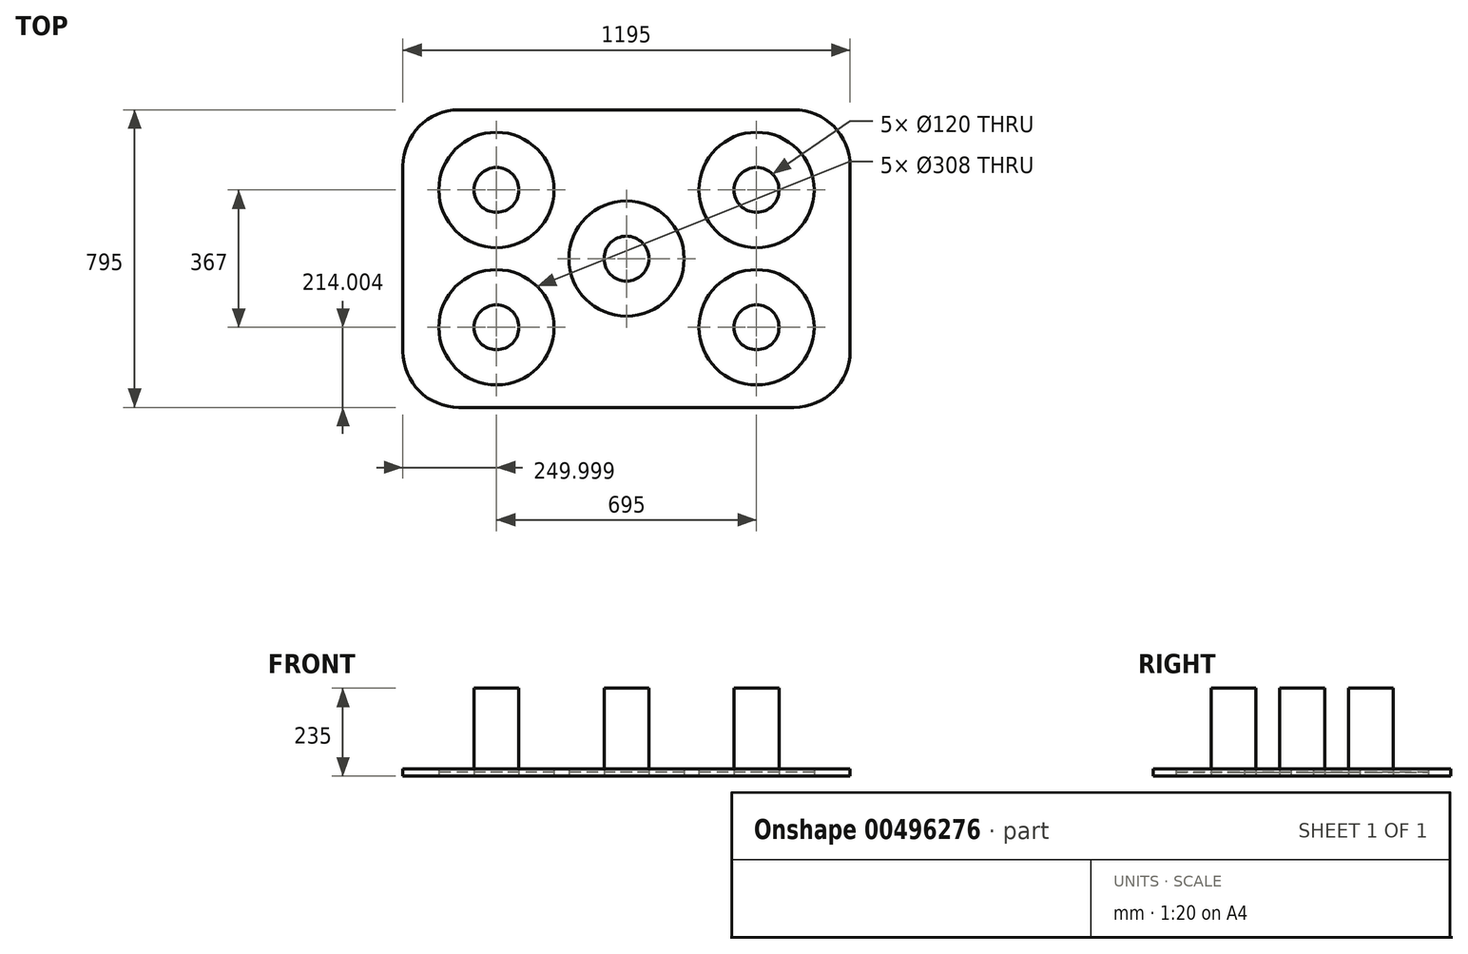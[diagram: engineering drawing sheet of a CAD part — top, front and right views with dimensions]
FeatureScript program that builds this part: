
annotation { "Feature Type Name" : "Feature", "Feature Type Description" : "" }
export const myFeature = defineFeature(function(context is Context, id is Id, definition is map)
    precondition{}
    {
        {
            var Q0;
            Q0=qCreatedBy(makeId("Top.planeOp"),FACE);
            var sketch = newSketch(context, id + "F0", { "sketchPlane" : qUnion([Q0])});
            skLineSegment(sketch, "E0.bottom", {"start": v(51.86, 514.27) * mm, "end": v(946.86, 514.27) * mm});
            skLineSegment(sketch, "E0.top", {"start": v(51.86, -280.73) * mm, "end": v(946.86, -280.73) * mm});
            skLineSegment(sketch, "E0.left", {"start": v(-98.14, 364.27) * mm, "end": v(-98.14, -130.73) * mm});
            skLineSegment(sketch, "E0.right", {"start": v(1096.86, 364.27) * mm, "end": v(1096.86, -130.73) * mm});
            skCircle(sketch, "E1", {"center": v(151.86, 300.27) * mm, "radius": 60 * mm});
            skCircle(sketch, "E2", {"center": v(846.86, -66.73) * mm, "radius": 60 * mm});
            skCircle(sketch, "E3", {"center": v(151.86, -66.73) * mm, "radius": 60 * mm});
            skCircle(sketch, "E4", {"center": v(846.86, 300.27) * mm, "radius": 60 * mm});
            skCircle(sketch, "E5", {"center": v(499.36, 116.77) * mm, "radius": 60 * mm});
            skPoint(sketch, "E6.visualSharp", {"position": v(-98.14, 514.27) * mm});
            skArc(sketch, "E6.filletArc", {"start": v(51.86, 514.27) * mm, "mid": v(-54.2, 470.34) * mm, "end": v(-98.14, 364.27) * mm});
            skPoint(sketch, "E7.visualSharp", {"position": v(1096.86, 514.27) * mm});
            skArc(sketch, "E7.filletArc", {"start": v(1096.86, 364.27) * mm, "mid": v(1052.92, 470.34) * mm, "end": v(946.86, 514.27) * mm});
            skPoint(sketch, "E8.visualSharp", {"position": v(1096.86, -280.73) * mm});
            skArc(sketch, "E8.filletArc", {"start": v(946.86, -280.73) * mm, "mid": v(1052.92, -236.8) * mm, "end": v(1096.86, -130.73) * mm});
            skPoint(sketch, "E9.visualSharp", {"position": v(-98.14, -280.73) * mm});
            skArc(sketch, "E9.filletArc", {"start": v(-98.14, -130.73) * mm, "mid": v(-54.2, -236.8) * mm, "end": v(51.86, -280.73) * mm});
            skCircle(sketch, "E10", {"center": v(151.86, 300.27) * mm, "radius": 154 * mm});
            skCircle(sketch, "E11", {"center": v(151.86, -66.73) * mm, "radius": 154 * mm});
            skCircle(sketch, "E12", {"center": v(499.36, 116.77) * mm, "radius": 154 * mm});
            skCircle(sketch, "E13", {"center": v(846.86, 300.27) * mm, "radius": 154 * mm});
            skCircle(sketch, "E14", {"center": v(846.86, -66.73) * mm, "radius": 154 * mm});
            skSolve(sketch);
        }
        {
            var Q0;
            Q0 = qSketchRegion(id + "F0", true);
            extrude(context, id + "F1", {"entities" : qUnion([Q0]), "depth" : 20 * mm, "offsetDistance" : 25 * mm});
        }
        {
            var Q0;
            Q0=makeQuery(id+"F0.imprint","IMPRINT",FACE,{"disambiguationData":[TD([[makeQuery(id+"F0.imprint","IMPRINT",EDGE,{"derivedFrom":sQuery(id+"F0.wireOp",EDGE,"E2")}),1.0]])]});
            var Q1;
            Q1=makeQuery(id+"F0.imprint","IMPRINT",FACE,{"disambiguationData":[TD([[makeQuery(id+"F0.imprint","IMPRINT",EDGE,{"derivedFrom":sQuery(id+"F0.wireOp",EDGE,"E4")}),1.0]])]});
            var Q2;
            Q2=makeQuery(id+"F0.imprint","IMPRINT",FACE,{"disambiguationData":[TD([[makeQuery(id+"F0.imprint","IMPRINT",EDGE,{"derivedFrom":sQuery(id+"F0.wireOp",EDGE,"E5")}),1.0]])]});
            var Q3;
            Q3=makeQuery(id+"F0.imprint","IMPRINT",FACE,{"disambiguationData":[TD([[makeQuery(id+"F0.imprint","IMPRINT",EDGE,{"derivedFrom":sQuery(id+"F0.wireOp",EDGE,"E3")}),1.0]])]});
            var Q4;
            Q4=makeQuery(id+"F0.imprint","IMPRINT",FACE,{"disambiguationData":[TD([[makeQuery(id+"F0.imprint","IMPRINT",EDGE,{"derivedFrom":sQuery(id+"F0.wireOp",EDGE,"E1")}),1.0]])]});
            extrude(context, id + "F2", {"entities" : qUnion([Q0, Q1, Q2, Q3, Q4]), "operationType" : NewBodyOperationType.ADD, "depth" : 235 * mm, "offsetDistance" : 25 * mm});
        }
        {
            var Q0;
            Q0=makeQuery(id+"F0.imprint","IMPRINT",FACE,{"disambiguationData":[TD([[makeQuery(id+"F0.imprint","IMPRINT",EDGE,{"derivedFrom":sQuery(id+"F0.wireOp",EDGE,"E1")}),-1.0]])]});
            var Q1;
            Q1=makeQuery(id+"F0.imprint","IMPRINT",FACE,{"disambiguationData":[TD([[makeQuery(id+"F0.imprint","IMPRINT",EDGE,{"derivedFrom":sQuery(id+"F0.wireOp",EDGE,"E3")}),-1.0]])]});
            var Q2;
            Q2=makeQuery(id+"F0.imprint","IMPRINT",FACE,{"disambiguationData":[TD([[makeQuery(id+"F0.imprint","IMPRINT",EDGE,{"derivedFrom":sQuery(id+"F0.wireOp",EDGE,"E5")}),-1.0]])]});
            var Q3;
            Q3=makeQuery(id+"F0.imprint","IMPRINT",FACE,{"disambiguationData":[TD([[makeQuery(id+"F0.imprint","IMPRINT",EDGE,{"derivedFrom":sQuery(id+"F0.wireOp",EDGE,"E4")}),-1.0]])]});
            var Q4;
            Q4=makeQuery(id+"F0.imprint","IMPRINT",FACE,{"disambiguationData":[TD([[makeQuery(id+"F0.imprint","IMPRINT",EDGE,{"derivedFrom":sQuery(id+"F0.wireOp",EDGE,"E2")}),-1.0]])]});
            extrude(context, id + "F3", {"entities" : qUnion([Q0, Q1, Q2, Q3, Q4]), "depth" : 10 * mm, "offsetDistance" : 25 * mm});
        }
    });
